# Revit family: Sink-Trap_Drain-KOHLER-K-9033T_1
name_source: partatom
category: Plumbing Fixtures
revit_build: Autodesk Revit 2017 (Build: 20160225_1515(x64)
units: mm (PartAtom-declared; Revit-internal decimal feet)

## family parameters
Cut with Voids When Loaded = No
Host = Face
OmniClass Number = 23.31.13.00
OmniClass Title = Sinks
Part Type = Normal
Room Calculation Point = No
Round Connector Dimension = Use Diameter
Shared = No

## types (5) — shared parameters
ADA Compliant = No
Assembly Code = D2010400
CW Connection = No
Cold Water Inlet = Cold Water Inlet
Date Modified = 10/07/2020
Default Elevation = 20"
Description = Wall-mounted drain elbow
Drain Included = No
HW Connection = No
Height = 5 1/16"
Hot Water Inlet = Hot Water Inlet
Length = 16 15/16"
Manufacturer = KOHLER Co.
Master Format 2014 = 22 41 16
Master Format 2014 Name = Residential Lavatories and Sinks
Material = Premium Metal Construction
Product Documentation Link = https://files.kohler.com.cn
Product Page URL = https://www.kohler.com.cn
URL = http://www.kohler.com.cn
Vent Connection = No
Waste Connection = Yes
Waste Water Inlet = Waste Water Inlet
Waste Water Outlet = Waste Water Outlet
WaterSense Certified = No
Width = 2 9/16"

## per-type parameters (varying)
| type | Finish | Model | Type |
| AF-French Gold | Kohler-Metal-AF-Vibrant_French_Gold | K-9033T-AF | 1 |
| SN-Polished Nickel | Kohler-Metal-SN-Vibrant_Polished_Nickel | K-9033T-SN | 2 |
| BN-Brushed Nickel | Kohler-Metal-BN-Vibrant_Brushed_Nickel | K-9033T-BN | 3 |
| BGD-Brushed Gold | Kohler-Metal-BGD-Vibrant_Moderne_Brushed_Gold | K-9033T-BGD | 4 |
| PGD-Polished Gold | Kohler-Metal-PGD-Modern_Polished_Gold | K-9033T-PGD | 5 |

## geometry (parser evidence)
native form markers: Sweep x5
no freeform markers — native parametric forms only
